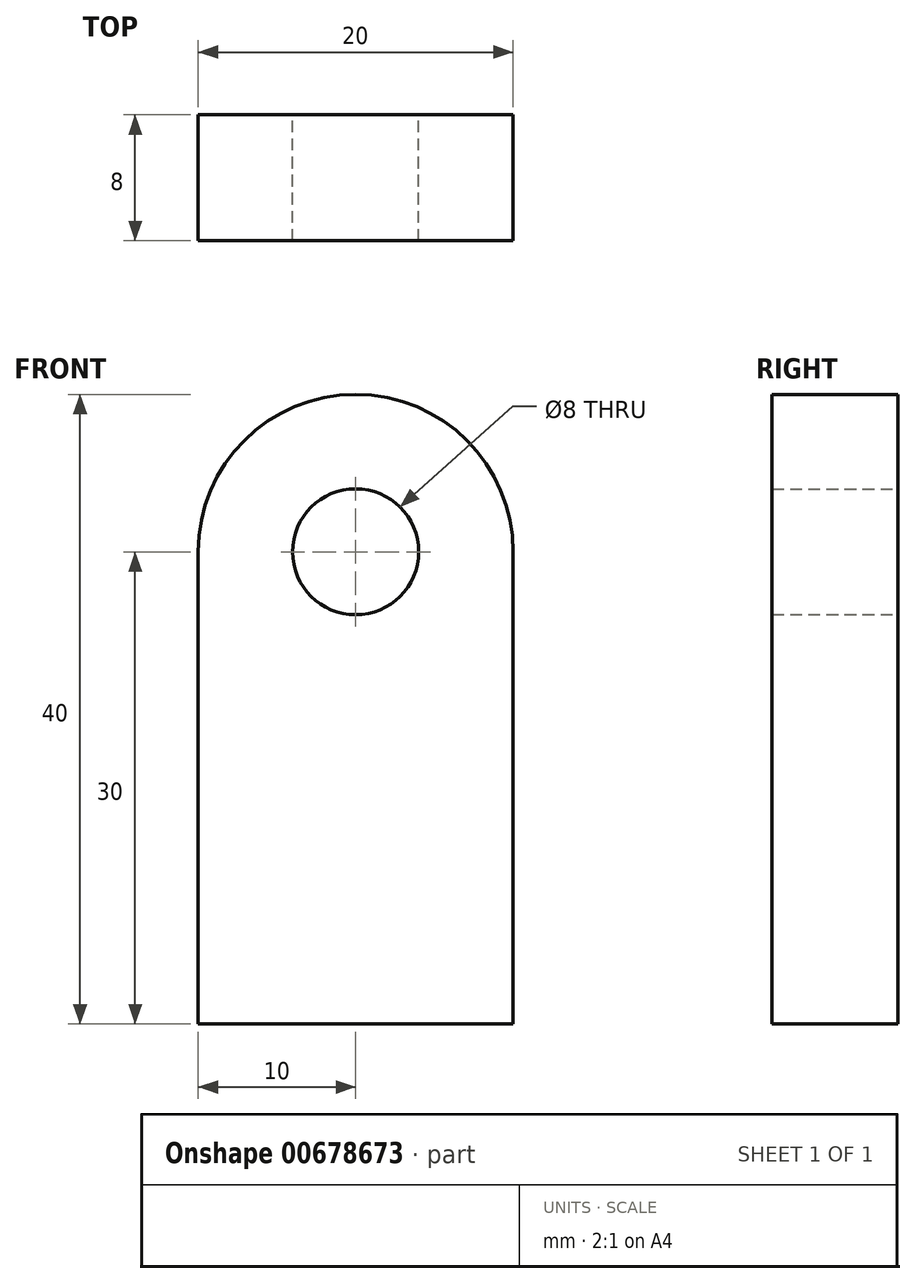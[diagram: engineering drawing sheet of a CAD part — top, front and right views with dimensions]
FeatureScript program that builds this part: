
annotation { "Feature Type Name" : "Feature", "Feature Type Description" : "" }
export const myFeature = defineFeature(function(context is Context, id is Id, definition is map)
    precondition{}
    {
        {
            var Q0;
            Q0=qCreatedBy(makeId("Front.planeOp"),FACE);
            var sketch = newSketch(context, id + "F0", { "sketchPlane" : qUnion([Q0])});
            skArc(sketch, "E0", {"start": v(10, 30) * mm, "mid": v(0, 40) * mm, "end": v(-10, 30) * mm});
            skCircle(sketch, "E1", {"center": v(0, 30) * mm, "radius": 4 * mm});
            skLineSegment(sketch, "E2", {"start": v(-10, 30) * mm, "end": v(-10, 0) * mm});
            skLineSegment(sketch, "E3", {"start": v(10, 30) * mm, "end": v(10, 0) * mm});
            skLineSegment(sketch, "E4", {"start": v(10, 0) * mm, "end": v(-10, 0) * mm});
            skSolve(sketch);
        }
        {
            var Q0;
            Q0 = qSketchRegion(id + "F0", true);
            extrude(context, id + "F1", {"entities" : qUnion([Q0]), "depth" : 8 * mm, "offsetDistance" : 25.4 * mm});
        }
    });
